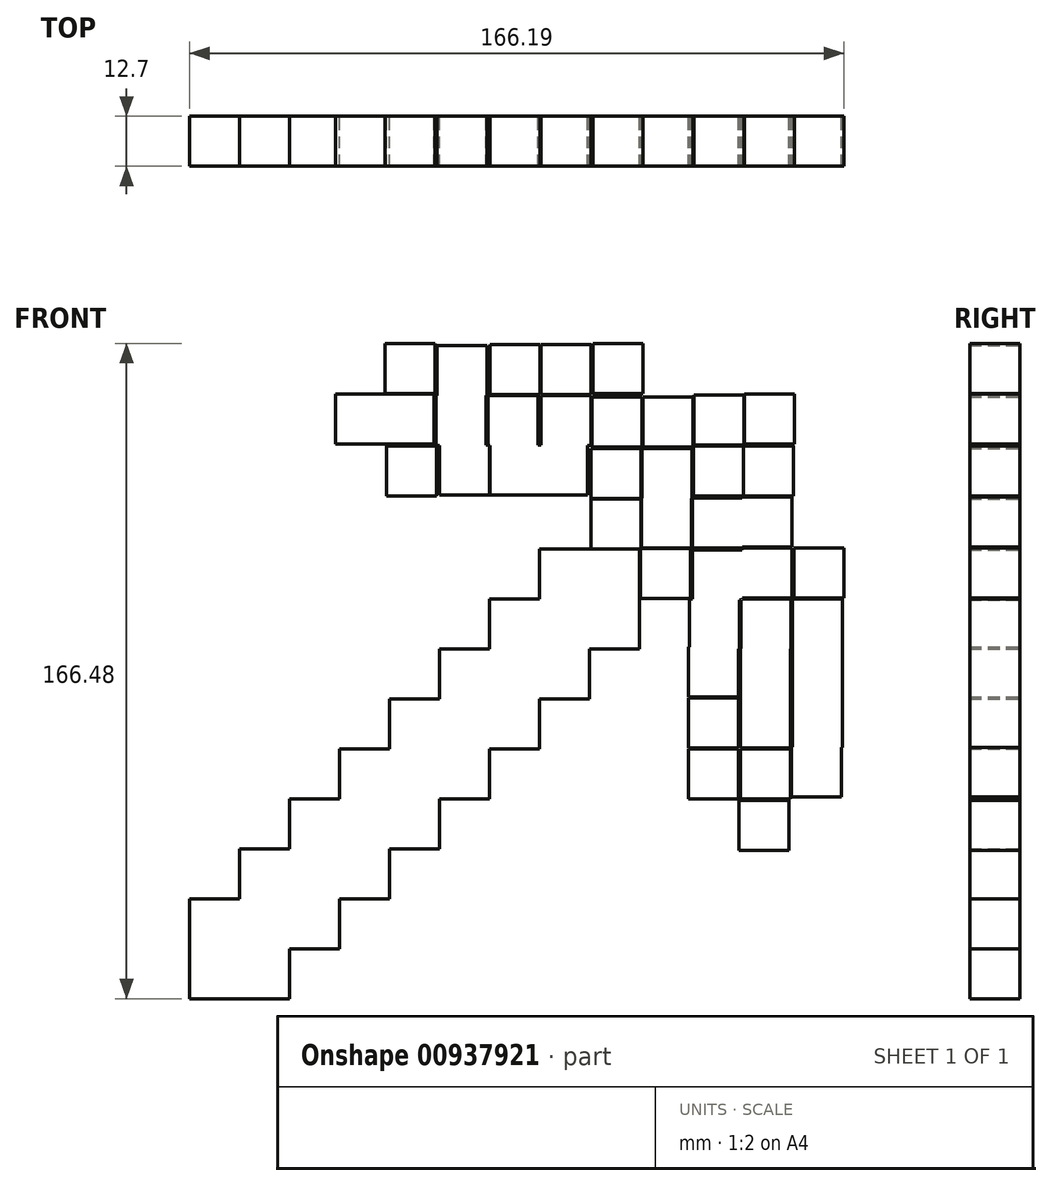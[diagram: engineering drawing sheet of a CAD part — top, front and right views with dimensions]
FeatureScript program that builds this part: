
annotation { "Feature Type Name" : "Feature", "Feature Type Description" : "" }
export const myFeature = defineFeature(function(context is Context, id is Id, definition is map)
    precondition{}
    {
        {
            var Q0;
            Q0=qCreatedBy(makeId("Front.planeOp"),FACE);
            var sketch = newSketch(context, id + "F0", { "sketchPlane" : qUnion([Q0])});
            skLineSegment(sketch, "E0.bottom", {"start": v(25.84, 1.28) * mm, "end": v(0.44, 1.28) * mm});
            skLineSegment(sketch, "E0.top", {"start": v(25.84, 26.68) * mm, "end": v(0.44, 26.68) * mm});
            skLineSegment(sketch, "E0.left", {"start": v(25.84, 1.28) * mm, "end": v(25.84, 26.68) * mm});
            skLineSegment(sketch, "E0.right", {"start": v(0.44, 1.28) * mm, "end": v(0.44, 26.68) * mm});
            skPoint(sketch, "E0.middle", {"position": v(13.14, 13.98) * mm});
            skLineSegment(sketch, "E1.bottom", {"start": v(-37.66, -62.22) * mm, "end": v(-63.06, -62.22) * mm});
            skLineSegment(sketch, "E1.top", {"start": v(-37.66, -36.82) * mm, "end": v(-63.06, -36.82) * mm});
            skLineSegment(sketch, "E1.left", {"start": v(-37.66, -62.22) * mm, "end": v(-37.66, -36.82) * mm});
            skLineSegment(sketch, "E1.right", {"start": v(-63.06, -62.22) * mm, "end": v(-63.06, -36.82) * mm});
            skPoint(sketch, "E1.middle", {"position": v(-50.36, -49.52) * mm});
            skLineSegment(sketch, "E2.bottom", {"start": v(51.24, 26.68) * mm, "end": v(25.84, 26.68) * mm});
            skLineSegment(sketch, "E2.top", {"start": v(51.24, 52.08) * mm, "end": v(25.84, 52.08) * mm});
            skLineSegment(sketch, "E2.left", {"start": v(51.24, 26.68) * mm, "end": v(51.24, 52.08) * mm});
            skLineSegment(sketch, "E2.right", {"start": v(25.84, 26.68) * mm, "end": v(25.84, 52.08) * mm});
            skPoint(sketch, "E2.middle", {"position": v(38.54, 39.38) * mm});
            skLineSegment(sketch, "E3.bottom", {"start": v(13.14, -11.42) * mm, "end": v(-12.26, -11.42) * mm});
            skLineSegment(sketch, "E3.top", {"start": v(13.14, 13.98) * mm, "end": v(-12.26, 13.98) * mm});
            skLineSegment(sketch, "E3.left", {"start": v(13.14, -11.42) * mm, "end": v(13.14, 13.98) * mm});
            skLineSegment(sketch, "E3.right", {"start": v(-12.26, -11.42) * mm, "end": v(-12.26, 13.98) * mm});
            skPoint(sketch, "E3.middle", {"position": v(0.44, 1.28) * mm});
            skLineSegment(sketch, "E4.bottom", {"start": v(-24.96, -49.52) * mm, "end": v(-50.36, -49.52) * mm});
            skLineSegment(sketch, "E4.top", {"start": v(-24.96, -24.12) * mm, "end": v(-50.36, -24.12) * mm});
            skLineSegment(sketch, "E4.left", {"start": v(-24.96, -49.52) * mm, "end": v(-24.96, -24.12) * mm});
            skLineSegment(sketch, "E4.right", {"start": v(-50.36, -49.52) * mm, "end": v(-50.36, -24.12) * mm});
            skPoint(sketch, "E4.middle", {"position": v(-37.66, -36.82) * mm});
            skLineSegment(sketch, "E5.bottom", {"start": v(-12.26, -36.82) * mm, "end": v(-37.66, -36.82) * mm});
            skLineSegment(sketch, "E5.top", {"start": v(-12.26, -11.42) * mm, "end": v(-37.66, -11.42) * mm});
            skLineSegment(sketch, "E5.left", {"start": v(-12.26, -36.82) * mm, "end": v(-12.26, -11.42) * mm});
            skLineSegment(sketch, "E5.right", {"start": v(-37.66, -36.82) * mm, "end": v(-37.66, -11.42) * mm});
            skPoint(sketch, "E5.middle", {"position": v(-24.96, -24.12) * mm});
            skLineSegment(sketch, "E6.bottom", {"start": v(38.54, 13.98) * mm, "end": v(13.14, 13.98) * mm});
            skLineSegment(sketch, "E6.top", {"start": v(38.54, 39.38) * mm, "end": v(13.14, 39.38) * mm});
            skLineSegment(sketch, "E6.left", {"start": v(38.54, 13.98) * mm, "end": v(38.54, 39.38) * mm});
            skLineSegment(sketch, "E6.right", {"start": v(13.14, 13.98) * mm, "end": v(13.14, 39.38) * mm});
            skPoint(sketch, "E6.middle", {"position": v(25.84, 26.68) * mm});
            skLineSegment(sketch, "E7.bottom", {"start": v(0.44, -24.12) * mm, "end": v(-24.96, -24.12) * mm});
            skLineSegment(sketch, "E7.top", {"start": v(0.44, 1.28) * mm, "end": v(-24.96, 1.28) * mm});
            skLineSegment(sketch, "E7.left", {"start": v(0.44, -24.12) * mm, "end": v(0.44, 1.28) * mm});
            skLineSegment(sketch, "E7.right", {"start": v(-24.96, -24.12) * mm, "end": v(-24.96, 1.28) * mm});
            skPoint(sketch, "E7.middle", {"position": v(-12.26, -11.42) * mm});
            skLineSegment(sketch, "E8.bottom", {"start": v(51.65, 52.09) * mm, "end": v(38.95, 52.09) * mm});
            skLineSegment(sketch, "E8.top", {"start": v(51.65, 64.79) * mm, "end": v(38.95, 64.79) * mm});
            skLineSegment(sketch, "E8.left", {"start": v(51.65, 52.09) * mm, "end": v(51.65, 64.79) * mm});
            skLineSegment(sketch, "E8.right", {"start": v(38.95, 52.09) * mm, "end": v(38.95, 64.79) * mm});
            skPoint(sketch, "E8.middle", {"position": v(45.3, 58.44) * mm});
            skLineSegment(sketch, "E9.bottom", {"start": v(51.6, 64.85) * mm, "end": v(38.9, 64.85) * mm});
            skLineSegment(sketch, "E9.top", {"start": v(51.6, 77.55) * mm, "end": v(38.9, 77.55) * mm});
            skLineSegment(sketch, "E9.left", {"start": v(51.6, 64.85) * mm, "end": v(51.6, 77.55) * mm});
            skLineSegment(sketch, "E9.right", {"start": v(38.9, 64.85) * mm, "end": v(38.9, 77.55) * mm});
            skPoint(sketch, "E9.middle", {"position": v(45.25, 71.2) * mm});
            skLineSegment(sketch, "E10.bottom", {"start": v(51.43, 39.44) * mm, "end": v(64.13, 39.44) * mm});
            skLineSegment(sketch, "E10.top", {"start": v(51.43, 52.14) * mm, "end": v(64.13, 52.14) * mm});
            skLineSegment(sketch, "E10.left", {"start": v(51.43, 39.44) * mm, "end": v(51.43, 52.14) * mm});
            skLineSegment(sketch, "E10.right", {"start": v(64.13, 39.44) * mm, "end": v(64.13, 52.14) * mm});
            skPoint(sketch, "E10.middle", {"position": v(57.78, 45.79) * mm});
            skLineSegment(sketch, "E11.bottom", {"start": v(64.4, 52.34) * mm, "end": v(51.7, 52.34) * mm});
            skLineSegment(sketch, "E11.top", {"start": v(64.4, 65.04) * mm, "end": v(51.7, 65.04) * mm});
            skLineSegment(sketch, "E11.left", {"start": v(64.4, 52.34) * mm, "end": v(64.4, 65.04) * mm});
            skLineSegment(sketch, "E11.right", {"start": v(51.7, 52.34) * mm, "end": v(51.7, 65.04) * mm});
            skPoint(sketch, "E11.middle", {"position": v(58.05, 58.7) * mm});
            skLineSegment(sketch, "E12.bottom", {"start": v(77.38, 39.1) * mm, "end": v(64.68, 39.1) * mm});
            skLineSegment(sketch, "E12.top", {"start": v(77.38, 51.8) * mm, "end": v(64.68, 51.8) * mm});
            skLineSegment(sketch, "E12.left", {"start": v(77.38, 39.1) * mm, "end": v(77.38, 51.8) * mm});
            skLineSegment(sketch, "E12.right", {"start": v(64.68, 39.1) * mm, "end": v(64.68, 51.8) * mm});
            skPoint(sketch, "E12.middle", {"position": v(71.03, 45.44) * mm});
            skLineSegment(sketch, "E13.bottom", {"start": v(51.9, 64.91) * mm, "end": v(64.6, 64.91) * mm});
            skLineSegment(sketch, "E13.top", {"start": v(51.9, 77.61) * mm, "end": v(64.6, 77.61) * mm});
            skLineSegment(sketch, "E13.left", {"start": v(51.9, 64.91) * mm, "end": v(51.9, 77.61) * mm});
            skLineSegment(sketch, "E13.right", {"start": v(64.6, 64.91) * mm, "end": v(64.6, 77.61) * mm});
            skPoint(sketch, "E13.middle", {"position": v(58.25, 71.26) * mm});
            skLineSegment(sketch, "E14.bottom", {"start": v(77.38, 52.34) * mm, "end": v(64.68, 52.34) * mm});
            skLineSegment(sketch, "E14.top", {"start": v(77.38, 65.04) * mm, "end": v(64.68, 65.04) * mm});
            skLineSegment(sketch, "E14.left", {"start": v(77.38, 52.34) * mm, "end": v(77.38, 65.04) * mm});
            skLineSegment(sketch, "E14.right", {"start": v(64.68, 52.34) * mm, "end": v(64.68, 65.04) * mm});
            skPoint(sketch, "E14.middle", {"position": v(71.03, 58.7) * mm});
            skLineSegment(sketch, "E15.bottom", {"start": v(64.88, 65.52) * mm, "end": v(77.58, 65.52) * mm});
            skLineSegment(sketch, "E15.top", {"start": v(64.88, 78.22) * mm, "end": v(77.58, 78.22) * mm});
            skLineSegment(sketch, "E15.left", {"start": v(64.88, 65.52) * mm, "end": v(64.88, 78.22) * mm});
            skLineSegment(sketch, "E15.right", {"start": v(77.58, 65.52) * mm, "end": v(77.58, 78.22) * mm});
            skPoint(sketch, "E15.middle", {"position": v(71.23, 71.87) * mm});
            skPoint(sketch, "E16", {"position": v(71.03, 51.8) * mm});
            skLineSegment(sketch, "E17.bottom", {"start": v(90.35, 65.52) * mm, "end": v(77.65, 65.52) * mm});
            skLineSegment(sketch, "E17.top", {"start": v(90.35, 78.22) * mm, "end": v(77.65, 78.22) * mm});
            skLineSegment(sketch, "E17.left", {"start": v(90.35, 65.52) * mm, "end": v(90.35, 78.22) * mm});
            skLineSegment(sketch, "E17.right", {"start": v(77.65, 65.52) * mm, "end": v(77.65, 78.22) * mm});
            skPoint(sketch, "E17.middle", {"position": v(84, 71.87) * mm});
            skLineSegment(sketch, "E18.bottom", {"start": v(90.55, 78.7) * mm, "end": v(77.85, 78.7) * mm});
            skLineSegment(sketch, "E18.top", {"start": v(90.55, 91.4) * mm, "end": v(77.85, 91.4) * mm});
            skLineSegment(sketch, "E18.left", {"start": v(90.55, 78.7) * mm, "end": v(90.55, 91.4) * mm});
            skLineSegment(sketch, "E18.right", {"start": v(77.85, 78.7) * mm, "end": v(77.85, 91.4) * mm});
            skPoint(sketch, "E18.middle", {"position": v(84.2, 85.05) * mm});
            skLineSegment(sketch, "E19.bottom", {"start": v(77.04, 26.6) * mm, "end": v(89.74, 26.6) * mm});
            skLineSegment(sketch, "E19.top", {"start": v(77.04, 39.3) * mm, "end": v(89.74, 39.3) * mm});
            skLineSegment(sketch, "E19.left", {"start": v(77.04, 26.6) * mm, "end": v(77.04, 39.3) * mm});
            skLineSegment(sketch, "E19.right", {"start": v(89.74, 26.6) * mm, "end": v(89.74, 39.3) * mm});
            skPoint(sketch, "E19.middle", {"position": v(83.4, 32.94) * mm});
            skLineSegment(sketch, "E20.bottom", {"start": v(89.54, 14.02) * mm, "end": v(76.84, 14.02) * mm});
            skLineSegment(sketch, "E20.top", {"start": v(89.54, 26.72) * mm, "end": v(76.84, 26.72) * mm});
            skLineSegment(sketch, "E20.left", {"start": v(89.54, 14.02) * mm, "end": v(89.54, 26.72) * mm});
            skLineSegment(sketch, "E20.right", {"start": v(76.84, 14.02) * mm, "end": v(76.84, 26.72) * mm});
            skPoint(sketch, "E20.middle", {"position": v(83.2, 20.37) * mm});
            skLineSegment(sketch, "E21.bottom", {"start": v(89.95, 39.57) * mm, "end": v(77.25, 39.57) * mm});
            skLineSegment(sketch, "E21.top", {"start": v(89.95, 52.27) * mm, "end": v(77.25, 52.27) * mm});
            skLineSegment(sketch, "E21.left", {"start": v(89.95, 39.57) * mm, "end": v(89.95, 52.27) * mm});
            skLineSegment(sketch, "E21.right", {"start": v(77.25, 39.57) * mm, "end": v(77.25, 52.27) * mm});
            skPoint(sketch, "E21.middle", {"position": v(83.6, 45.92) * mm});
            skLineSegment(sketch, "E22.bottom", {"start": v(89.54, 1.45) * mm, "end": v(76.84, 1.45) * mm});
            skLineSegment(sketch, "E22.top", {"start": v(89.54, 14.15) * mm, "end": v(76.84, 14.15) * mm});
            skLineSegment(sketch, "E22.left", {"start": v(89.54, 1.45) * mm, "end": v(89.54, 14.15) * mm});
            skLineSegment(sketch, "E22.right", {"start": v(76.84, 1.45) * mm, "end": v(76.84, 14.15) * mm});
            skPoint(sketch, "E22.middle", {"position": v(83.2, 7.8) * mm});
            skLineSegment(sketch, "E23.bottom", {"start": v(76.84, -11.53) * mm, "end": v(89.54, -11.53) * mm});
            skLineSegment(sketch, "E23.top", {"start": v(76.84, 1.17) * mm, "end": v(89.54, 1.17) * mm});
            skLineSegment(sketch, "E23.left", {"start": v(76.84, -11.53) * mm, "end": v(76.84, 1.17) * mm});
            skLineSegment(sketch, "E23.right", {"start": v(89.54, -11.53) * mm, "end": v(89.54, 1.17) * mm});
            skPoint(sketch, "E23.middle", {"position": v(83.2, -5.18) * mm});
            skLineSegment(sketch, "E24.bottom", {"start": v(77.78, 78.5) * mm, "end": v(65.08, 78.5) * mm});
            skLineSegment(sketch, "E24.top", {"start": v(77.78, 91.2) * mm, "end": v(65.08, 91.2) * mm});
            skLineSegment(sketch, "E24.left", {"start": v(77.78, 78.5) * mm, "end": v(77.78, 91.2) * mm});
            skLineSegment(sketch, "E24.right", {"start": v(65.08, 78.5) * mm, "end": v(65.08, 91.2) * mm});
            skPoint(sketch, "E24.middle", {"position": v(71.43, 84.85) * mm});
            skLineSegment(sketch, "E25.bottom", {"start": v(89.95, 52.55) * mm, "end": v(77.25, 52.55) * mm});
            skLineSegment(sketch, "E25.top", {"start": v(89.95, 65.25) * mm, "end": v(77.25, 65.25) * mm});
            skLineSegment(sketch, "E25.left", {"start": v(89.95, 52.55) * mm, "end": v(89.95, 65.25) * mm});
            skLineSegment(sketch, "E25.right", {"start": v(77.25, 52.55) * mm, "end": v(77.25, 65.25) * mm});
            skPoint(sketch, "E25.middle", {"position": v(83.6, 58.9) * mm});
            skLineSegment(sketch, "E26.bottom", {"start": v(64.8, 77.9) * mm, "end": v(52.1, 77.9) * mm});
            skLineSegment(sketch, "E26.top", {"start": v(64.8, 90.6) * mm, "end": v(52.1, 90.6) * mm});
            skLineSegment(sketch, "E26.left", {"start": v(64.8, 77.9) * mm, "end": v(64.8, 90.6) * mm});
            skLineSegment(sketch, "E26.right", {"start": v(52.1, 77.9) * mm, "end": v(52.1, 90.6) * mm});
            skPoint(sketch, "E26.middle", {"position": v(58.45, 84.24) * mm});
            skLineSegment(sketch, "E27.bottom", {"start": v(102.72, 14.22) * mm, "end": v(90.02, 14.22) * mm});
            skLineSegment(sketch, "E27.top", {"start": v(102.72, 26.92) * mm, "end": v(90.02, 26.92) * mm});
            skLineSegment(sketch, "E27.left", {"start": v(102.72, 14.22) * mm, "end": v(102.72, 26.92) * mm});
            skLineSegment(sketch, "E27.right", {"start": v(90.02, 14.22) * mm, "end": v(90.02, 26.92) * mm});
            skPoint(sketch, "E27.middle", {"position": v(96.37, 20.57) * mm});
            skLineSegment(sketch, "E28.bottom", {"start": v(89.14, -24.5) * mm, "end": v(76.44, -24.5) * mm});
            skLineSegment(sketch, "E28.top", {"start": v(89.14, -11.8) * mm, "end": v(76.44, -11.8) * mm});
            skLineSegment(sketch, "E28.left", {"start": v(89.14, -24.5) * mm, "end": v(89.14, -11.8) * mm});
            skLineSegment(sketch, "E28.right", {"start": v(76.44, -24.5) * mm, "end": v(76.44, -11.8) * mm});
            skPoint(sketch, "E28.middle", {"position": v(82.79, -18.15) * mm});
            skLineSegment(sketch, "E29.bottom", {"start": v(76.36, 14.43) * mm, "end": v(63.66, 14.43) * mm});
            skLineSegment(sketch, "E29.top", {"start": v(76.36, 27.13) * mm, "end": v(63.66, 27.13) * mm});
            skLineSegment(sketch, "E29.left", {"start": v(76.36, 14.43) * mm, "end": v(76.36, 27.13) * mm});
            skLineSegment(sketch, "E29.right", {"start": v(63.66, 14.43) * mm, "end": v(63.66, 27.13) * mm});
            skPoint(sketch, "E29.middle", {"position": v(70.01, 20.78) * mm});
            skLineSegment(sketch, "E30.bottom", {"start": v(76.57, 26.6) * mm, "end": v(63.87, 26.6) * mm});
            skLineSegment(sketch, "E30.top", {"start": v(76.57, 39.3) * mm, "end": v(63.87, 39.3) * mm});
            skLineSegment(sketch, "E30.left", {"start": v(76.57, 26.6) * mm, "end": v(76.57, 39.3) * mm});
            skLineSegment(sketch, "E30.right", {"start": v(63.87, 26.6) * mm, "end": v(63.87, 39.3) * mm});
            skPoint(sketch, "E30.middle", {"position": v(70.22, 32.94) * mm});
            skLineSegment(sketch, "E31.bottom", {"start": v(102.52, -10.92) * mm, "end": v(89.82, -10.92) * mm});
            skLineSegment(sketch, "E31.top", {"start": v(102.52, 1.78) * mm, "end": v(89.82, 1.78) * mm});
            skLineSegment(sketch, "E31.left", {"start": v(102.52, -10.92) * mm, "end": v(102.52, 1.78) * mm});
            skLineSegment(sketch, "E31.right", {"start": v(89.82, -10.92) * mm, "end": v(89.82, 1.78) * mm});
            skPoint(sketch, "E31.middle", {"position": v(96.17, -4.57) * mm});
            skLineSegment(sketch, "E32.bottom", {"start": v(102.72, 26.6) * mm, "end": v(90.02, 26.6) * mm});
            skLineSegment(sketch, "E32.top", {"start": v(102.72, 39.3) * mm, "end": v(90.02, 39.3) * mm});
            skLineSegment(sketch, "E32.left", {"start": v(102.72, 26.6) * mm, "end": v(102.72, 39.3) * mm});
            skLineSegment(sketch, "E32.right", {"start": v(90.02, 26.6) * mm, "end": v(90.02, 39.3) * mm});
            skPoint(sketch, "E32.middle", {"position": v(96.37, 32.94) * mm});
            skLineSegment(sketch, "E33.bottom", {"start": v(102.72, 1.65) * mm, "end": v(90.02, 1.65) * mm});
            skLineSegment(sketch, "E33.top", {"start": v(102.72, 14.35) * mm, "end": v(90.02, 14.35) * mm});
            skLineSegment(sketch, "E33.left", {"start": v(102.72, 1.65) * mm, "end": v(102.72, 14.35) * mm});
            skLineSegment(sketch, "E33.right", {"start": v(90.02, 1.65) * mm, "end": v(90.02, 14.35) * mm});
            skPoint(sketch, "E33.middle", {"position": v(96.37, 8) * mm});
            skLineSegment(sketch, "E34.bottom", {"start": v(76.36, -11.53) * mm, "end": v(63.66, -11.53) * mm});
            skLineSegment(sketch, "E34.top", {"start": v(76.36, 1.17) * mm, "end": v(63.66, 1.17) * mm});
            skLineSegment(sketch, "E34.left", {"start": v(76.36, -11.53) * mm, "end": v(76.36, 1.17) * mm});
            skLineSegment(sketch, "E34.right", {"start": v(63.66, -11.53) * mm, "end": v(63.66, 1.17) * mm});
            skPoint(sketch, "E34.middle", {"position": v(70.01, -5.18) * mm});
            skLineSegment(sketch, "E35.bottom", {"start": v(76.36, 1.45) * mm, "end": v(63.66, 1.45) * mm});
            skLineSegment(sketch, "E35.top", {"start": v(76.36, 14.15) * mm, "end": v(63.66, 14.15) * mm});
            skLineSegment(sketch, "E35.left", {"start": v(76.36, 1.45) * mm, "end": v(76.36, 14.15) * mm});
            skLineSegment(sketch, "E35.right", {"start": v(63.66, 1.45) * mm, "end": v(63.66, 14.15) * mm});
            skPoint(sketch, "E35.middle", {"position": v(70.01, 7.8) * mm});
            skLineSegment(sketch, "E36.bottom", {"start": v(38.88, 78.37) * mm, "end": v(26.18, 78.37) * mm});
            skLineSegment(sketch, "E36.top", {"start": v(38.88, 91.07) * mm, "end": v(26.18, 91.07) * mm});
            skLineSegment(sketch, "E36.left", {"start": v(38.88, 78.37) * mm, "end": v(38.88, 91.07) * mm});
            skLineSegment(sketch, "E36.right", {"start": v(26.18, 78.37) * mm, "end": v(26.18, 91.07) * mm});
            skPoint(sketch, "E36.middle", {"position": v(32.53, 84.72) * mm});
            skLineSegment(sketch, "E37.bottom", {"start": v(25.4, 78.37) * mm, "end": v(12.7, 78.37) * mm});
            skLineSegment(sketch, "E37.top", {"start": v(25.4, 91.07) * mm, "end": v(12.7, 91.07) * mm});
            skLineSegment(sketch, "E37.left", {"start": v(25.4, 78.37) * mm, "end": v(25.4, 91.07) * mm});
            skLineSegment(sketch, "E37.right", {"start": v(12.7, 78.37) * mm, "end": v(12.7, 91.07) * mm});
            skPoint(sketch, "E37.middle", {"position": v(19.05, 84.72) * mm});
            skLineSegment(sketch, "E38.bottom", {"start": v(51.83, 77.9) * mm, "end": v(39.13, 77.9) * mm});
            skLineSegment(sketch, "E38.top", {"start": v(51.83, 90.6) * mm, "end": v(39.13, 90.6) * mm});
            skLineSegment(sketch, "E38.left", {"start": v(51.83, 77.9) * mm, "end": v(51.83, 90.6) * mm});
            skLineSegment(sketch, "E38.right", {"start": v(39.13, 77.9) * mm, "end": v(39.13, 90.6) * mm});
            skPoint(sketch, "E38.middle", {"position": v(45.48, 84.24) * mm});
            skLineSegment(sketch, "E39.bottom", {"start": v(-13.3, 78.66) * mm, "end": v(-26, 78.66) * mm});
            skLineSegment(sketch, "E39.top", {"start": v(-13.3, 91.36) * mm, "end": v(-26, 91.36) * mm});
            skLineSegment(sketch, "E39.left", {"start": v(-13.3, 78.66) * mm, "end": v(-13.3, 91.36) * mm});
            skLineSegment(sketch, "E39.right", {"start": v(-26, 78.66) * mm, "end": v(-26, 91.36) * mm});
            skPoint(sketch, "E39.middle", {"position": v(-19.66, 85) * mm});
            skLineSegment(sketch, "E40.bottom", {"start": v(-0.98, 78.66) * mm, "end": v(-13.68, 78.66) * mm});
            skLineSegment(sketch, "E40.top", {"start": v(-0.98, 91.36) * mm, "end": v(-13.68, 91.36) * mm});
            skLineSegment(sketch, "E40.left", {"start": v(-0.98, 78.66) * mm, "end": v(-0.98, 91.36) * mm});
            skLineSegment(sketch, "E40.right", {"start": v(-13.68, 78.66) * mm, "end": v(-13.68, 91.36) * mm});
            skPoint(sketch, "E40.middle", {"position": v(-7.33, 85) * mm});
            skLineSegment(sketch, "E41.bottom", {"start": v(-0.4, 65.47) * mm, "end": v(-13.1, 65.47) * mm});
            skLineSegment(sketch, "E41.top", {"start": v(-0.4, 78.17) * mm, "end": v(-13.1, 78.17) * mm});
            skLineSegment(sketch, "E41.left", {"start": v(-0.4, 65.47) * mm, "end": v(-0.4, 78.17) * mm});
            skLineSegment(sketch, "E41.right", {"start": v(-13.1, 65.47) * mm, "end": v(-13.1, 78.17) * mm});
            skPoint(sketch, "E41.middle", {"position": v(-6.75, 71.82) * mm});
            skLineSegment(sketch, "E42.bottom", {"start": v(12.21, 78.37) * mm, "end": v(-0.49, 78.37) * mm});
            skLineSegment(sketch, "E42.top", {"start": v(12.21, 91.07) * mm, "end": v(-0.49, 91.07) * mm});
            skLineSegment(sketch, "E42.left", {"start": v(12.21, 78.37) * mm, "end": v(12.21, 91.07) * mm});
            skLineSegment(sketch, "E42.right", {"start": v(-0.49, 78.37) * mm, "end": v(-0.49, 91.07) * mm});
            skPoint(sketch, "E42.middle", {"position": v(5.86, 84.72) * mm});
            skLineSegment(sketch, "E43.bottom", {"start": v(13.07, 65.75) * mm, "end": v(0.37, 65.75) * mm});
            skLineSegment(sketch, "E43.top", {"start": v(13.07, 78.45) * mm, "end": v(0.37, 78.45) * mm});
            skLineSegment(sketch, "E43.left", {"start": v(13.07, 65.75) * mm, "end": v(13.07, 78.45) * mm});
            skLineSegment(sketch, "E43.right", {"start": v(0.37, 65.75) * mm, "end": v(0.37, 78.45) * mm});
            skPoint(sketch, "E43.middle", {"position": v(6.72, 72.1) * mm});
            skLineSegment(sketch, "E44.bottom", {"start": v(103.13, 39.57) * mm, "end": v(90.43, 39.57) * mm});
            skLineSegment(sketch, "E44.top", {"start": v(103.13, 52.27) * mm, "end": v(90.43, 52.27) * mm});
            skLineSegment(sketch, "E44.left", {"start": v(103.13, 39.57) * mm, "end": v(103.13, 52.27) * mm});
            skLineSegment(sketch, "E44.right", {"start": v(90.43, 39.57) * mm, "end": v(90.43, 52.27) * mm});
            skPoint(sketch, "E44.middle", {"position": v(96.78, 45.92) * mm});
            skLineSegment(sketch, "E45.bottom", {"start": v(38.02, 65.75) * mm, "end": v(25.32, 65.75) * mm});
            skLineSegment(sketch, "E45.top", {"start": v(38.02, 78.45) * mm, "end": v(25.32, 78.45) * mm});
            skLineSegment(sketch, "E45.left", {"start": v(38.02, 65.75) * mm, "end": v(38.02, 78.45) * mm});
            skLineSegment(sketch, "E45.right", {"start": v(25.32, 65.75) * mm, "end": v(25.32, 78.45) * mm});
            skPoint(sketch, "E45.middle", {"position": v(31.67, 72.1) * mm});
            skLineSegment(sketch, "E46.bottom", {"start": v(25.98, 91.27) * mm, "end": v(13.28, 91.27) * mm});
            skLineSegment(sketch, "E46.top", {"start": v(25.98, 103.97) * mm, "end": v(13.28, 103.97) * mm});
            skLineSegment(sketch, "E46.left", {"start": v(25.98, 91.27) * mm, "end": v(25.98, 103.97) * mm});
            skLineSegment(sketch, "E46.right", {"start": v(13.28, 91.27) * mm, "end": v(13.28, 103.97) * mm});
            skPoint(sketch, "E46.middle", {"position": v(19.63, 97.62) * mm});
            skLineSegment(sketch, "E47.bottom", {"start": v(-0.7, 91.56) * mm, "end": v(-13.4, 91.56) * mm});
            skLineSegment(sketch, "E47.top", {"start": v(-0.7, 104.26) * mm, "end": v(-13.4, 104.26) * mm});
            skLineSegment(sketch, "E47.left", {"start": v(-0.7, 91.56) * mm, "end": v(-0.7, 104.26) * mm});
            skLineSegment(sketch, "E47.right", {"start": v(-13.4, 91.56) * mm, "end": v(-13.4, 104.26) * mm});
            skPoint(sketch, "E47.middle", {"position": v(-7.04, 97.9) * mm});
            skLineSegment(sketch, "E48.bottom", {"start": v(52.07, 91.56) * mm, "end": v(39.37, 91.56) * mm});
            skLineSegment(sketch, "E48.top", {"start": v(52.07, 104.26) * mm, "end": v(39.37, 104.26) * mm});
            skLineSegment(sketch, "E48.left", {"start": v(52.07, 91.56) * mm, "end": v(52.07, 104.26) * mm});
            skLineSegment(sketch, "E48.right", {"start": v(39.37, 91.56) * mm, "end": v(39.37, 104.26) * mm});
            skPoint(sketch, "E48.middle", {"position": v(45.72, 97.9) * mm});
            skLineSegment(sketch, "E49.bottom", {"start": v(25.98, 65.75) * mm, "end": v(13.28, 65.75) * mm});
            skLineSegment(sketch, "E49.top", {"start": v(25.98, 78.45) * mm, "end": v(13.28, 78.45) * mm});
            skLineSegment(sketch, "E49.left", {"start": v(25.98, 65.75) * mm, "end": v(25.98, 78.45) * mm});
            skLineSegment(sketch, "E49.right", {"start": v(13.28, 65.75) * mm, "end": v(13.28, 78.45) * mm});
            skPoint(sketch, "E49.middle", {"position": v(19.63, 72.1) * mm});
            skLineSegment(sketch, "E50.bottom", {"start": v(12.5, 90.99) * mm, "end": v(-0.2, 90.99) * mm});
            skLineSegment(sketch, "E50.top", {"start": v(12.5, 103.69) * mm, "end": v(-0.2, 103.69) * mm});
            skLineSegment(sketch, "E50.left", {"start": v(12.5, 90.99) * mm, "end": v(12.5, 103.69) * mm});
            skLineSegment(sketch, "E50.right", {"start": v(-0.2, 90.99) * mm, "end": v(-0.2, 103.69) * mm});
            skPoint(sketch, "E50.middle", {"position": v(6.15, 97.34) * mm});
            skLineSegment(sketch, "E51.bottom", {"start": v(38.88, 91.27) * mm, "end": v(26.18, 91.27) * mm});
            skLineSegment(sketch, "E51.top", {"start": v(38.88, 103.97) * mm, "end": v(26.18, 103.97) * mm});
            skLineSegment(sketch, "E51.left", {"start": v(38.88, 91.27) * mm, "end": v(38.88, 103.97) * mm});
            skLineSegment(sketch, "E51.right", {"start": v(26.18, 91.27) * mm, "end": v(26.18, 103.97) * mm});
            skPoint(sketch, "E51.middle", {"position": v(32.53, 97.62) * mm});
            skSolve(sketch);
        }
        {
            var Q0;
            Q0 = qSketchRegion(id + "F0", true);
            extrude(context, id + "F1", {"entities" : qUnion([Q0]), "depth" : 12.7 * mm, "offsetDistance" : 25.4 * mm});
        }
    });
